# Revit family: Elbow-B-Inox-Conex-15-54mm-PS5001 & PC5040
name_source: partatom
category: Pipe Fittings
units: mm (PartAtom-declared; Revit-internal decimal feet)

## family parameters
Always vertical = Yes
Cut with Voids When Loaded = No
OmniClass Number = 23.60.30.11.14
OmniClass Title = Pipework Fittings
Part Type = Elbow
Round Connector Dimension = Use Diameter
Shared = No
Work Plane-Based = No

## types (1)
- Standard
    Assembly Code = D2090800
    ConnectorTolerance = 2.00°
    Description = >B< Press Inox is a quick and simple to install flame-free fitting, manufactured using high quality hygienic stainless steel materials, suitable for multiple applications.
    K Coefficient Table = Regular 45, 90 and 180 Elbow
    Lookup Table Name = Elbow-B-Inox-Conex-15-54mm-PS5001 & PC5040
    Loss Method = K Coefficient from Table
    Manufacturer = Conex | Bänninger
    Material = Stainless Steel AISI 317
    Model = Elbow
    Model Specification = BMA
    Model Version = 2015
    ModifiedIssue_ANZRS = 20161226.54 $
    NATSPECWorkSection = TBC
    OmniclassProducts = TBC
    Type Comments = TBC
    URL = http://www.conexbanninger.com
    Uniformat IIElements = TBC

## geometry (parser evidence)
native form markers: Sweep x3
no freeform markers — native parametric forms only
